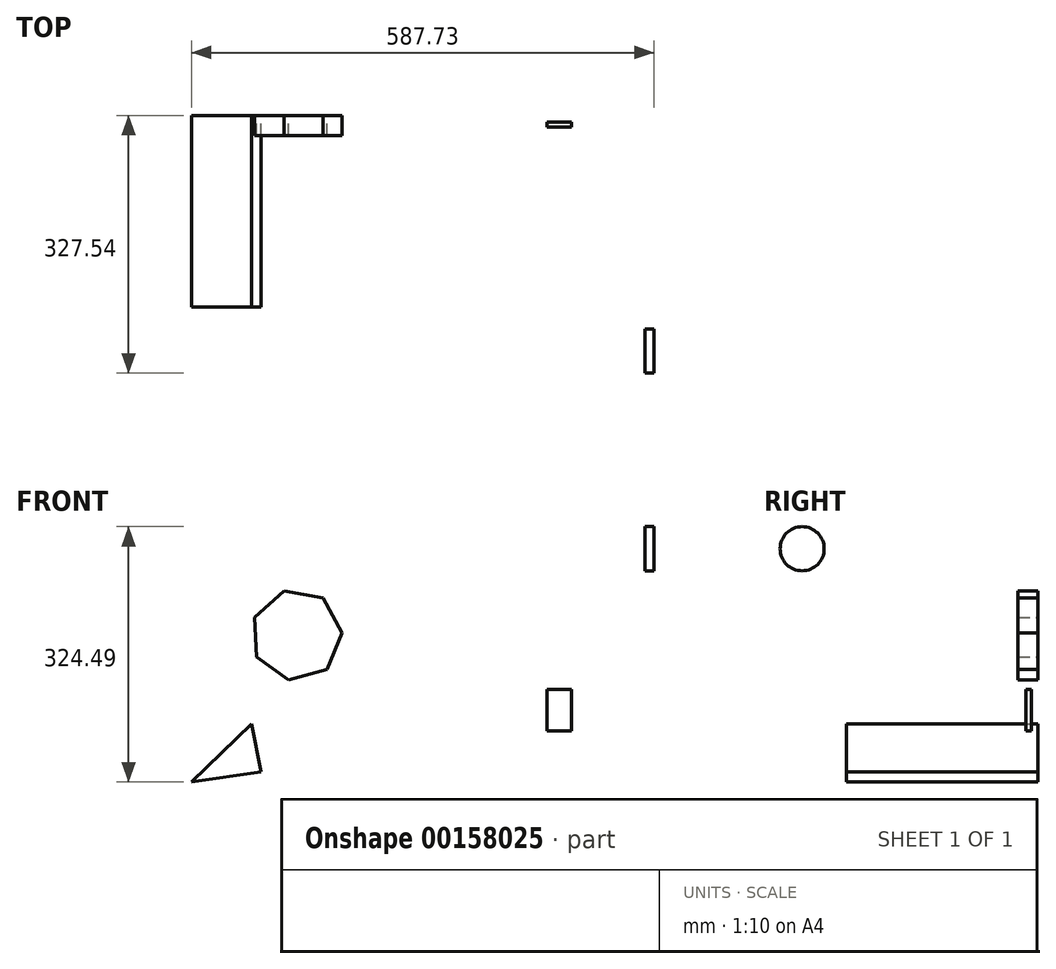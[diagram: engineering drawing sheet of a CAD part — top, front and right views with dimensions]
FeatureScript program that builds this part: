
annotation { "Feature Type Name" : "Feature", "Feature Type Description" : "" }
export const myFeature = defineFeature(function(context is Context, id is Id, definition is map)
    precondition{}
    {
        {
            var Q0;
            Q0=qCreatedBy(makeId("Top.planeOp"),FACE);
            var sketch = newSketch(context, id + "F0", { "sketchPlane" : qUnion([Q0])});
            skLineSegment(sketch, "E0.bottom", {"start": v(-124.58, -15.02) * mm, "end": v(-93.53, -15.02) * mm});
            skLineSegment(sketch, "E0.top", {"start": v(-124.58, -8.23) * mm, "end": v(-93.53, -8.23) * mm});
            skLineSegment(sketch, "E0.left", {"start": v(-124.58, -15.02) * mm, "end": v(-124.58, -8.23) * mm});
            skLineSegment(sketch, "E0.right", {"start": v(-93.53, -15.02) * mm, "end": v(-93.53, -8.23) * mm});
            skSolve(sketch);
        }
        {
            var Q0;
            Q0=makeQuery(id+"F0.imprint","IMPRINT",FACE,{"disambiguationData":[TD([[makeQuery(id+"F0.imprint","IMPRINT",EDGE,{"derivedFrom":sQuery(id+"F0.wireOp",EDGE,"E0.bottom")}),1.0]])]});
            extrude(context, id + "F1", {"entities" : qUnion([Q0]), "depth" : 52.7 * mm});
        }
        {
            var Q0;
            Q0=qCreatedBy(makeId("Right.planeOp"),FACE);
            var sketch = newSketch(context, id + "F2", { "sketchPlane" : qUnion([Q0])});
            skCircle(sketch, "E1", {"center": v(-299.54, 231.63) * mm, "radius": 28 * mm});
            skSolve(sketch);
        }
        {
            var Q0;
            Q0=makeQuery(id+"F2.imprint","IMPRINT",FACE,{"disambiguationData":[TD([[makeQuery(id+"F2.imprint","IMPRINT",EDGE,{"derivedFrom":sQuery(id+"F2.wireOp",EDGE,"E1")}),1.0]])]});
            extrude(context, id + "F3", {"entities" : qUnion([Q0]), "depth" : 11.43 * mm});
        }
        {
            var Q0;
            Q0=qCreatedBy(makeId("Front.planeOp"),FACE);
            var sketch = newSketch(context, id + "F4", { "sketchPlane" : qUnion([Q0])});
            skLineSegment(sketch, "E2", {"start": v(-577.47, -66) * mm, "end": v(-500.1, 9.35) * mm});
            skLineSegment(sketch, "E3", {"start": v(-500.1, 9.35) * mm, "end": v(-487.92, -51.61) * mm});
            skLineSegment(sketch, "E4", {"start": v(-583.92, -66) * mm, "end": v(-487.92, -51.61) * mm});
            skSolve(sketch);
        }
        {
            var Q0;
            {var subQ0=sQuery(id+"F4.wireOp",EDGE,"E3");Q0=makeQuery(id+"F4.imprint","IMPRINT",FACE,{"disambiguationData":[TD([[makeQuery(id+"F4.imprint","IMPRINT",EDGE,{"derivedFrom":subQ0}),-1.0]])]});}
            extrude(context, id + "F5", {"entities" : qUnion([Q0]), "depth" : 243.2 * mm});
        }
        {
            var Q0;
            Q0=qCreatedBy(makeId("Front.planeOp"),FACE);
            var sketch = newSketch(context, id + "F6", { "sketchPlane" : qUnion([Q0])});
            skCircle(sketch, "E5.cCircle", {"center": v(-442.78, 121.9) * mm, "radius": 52.31 * mm, "construction": true});
            skLineSegment(sketch, "E5.0", {"start": v(-404.22, 78.49) * mm, "end": v(-452.68, 64.69) * mm});
            skLineSegment(sketch, "E5.1", {"start": v(-452.68, 64.69) * mm, "end": v(-493.68, 93.97) * mm});
            skLineSegment(sketch, "E5.2", {"start": v(-493.68, 93.97) * mm, "end": v(-496.36, 144.28) * mm});
            skLineSegment(sketch, "E5.3", {"start": v(-496.36, 144.28) * mm, "end": v(-458.68, 177.74) * mm});
            skLineSegment(sketch, "E5.4", {"start": v(-458.68, 177.74) * mm, "end": v(-409.04, 169.15) * mm});
            skLineSegment(sketch, "E5.5", {"start": v(-409.04, 169.15) * mm, "end": v(-384.8, 124.98) * mm});
            skLineSegment(sketch, "E5.6", {"start": v(-384.8, 124.98) * mm, "end": v(-404.22, 78.49) * mm});
            skPoint(sketch, "E5.0.midPoint", {"position": v(-428.45, 71.59) * mm});
            skSolve(sketch);
        }
        {
            var Q0;
            Q0=makeQuery(id+"F6.imprint","IMPRINT",FACE,{"disambiguationData":[TD([[makeQuery(id+"F6.imprint","IMPRINT",EDGE,{"derivedFrom":sQuery(id+"F6.wireOp",EDGE,"E5.0")}),-1.0]])]});
            extrude(context, id + "F7", {"entities" : qUnion([Q0]), "depth" : 25.4 * mm});
        }
    });
